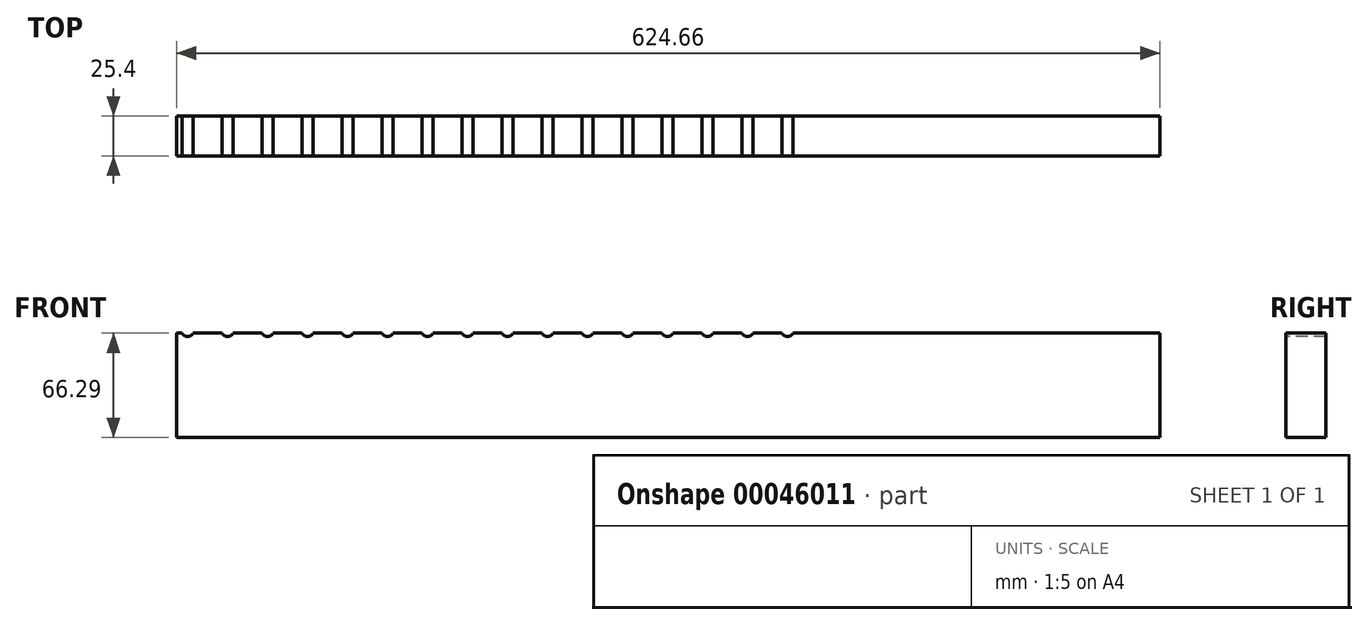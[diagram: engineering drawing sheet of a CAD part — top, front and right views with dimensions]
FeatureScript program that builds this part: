
annotation { "Feature Type Name" : "Feature", "Feature Type Description" : "" }
export const myFeature = defineFeature(function(context is Context, id is Id, definition is map)
    precondition{}
    {
        {
            var Q0;
            Q0=qCreatedBy(makeId("Front.planeOp"),FACE);
            var sketch = newSketch(context, id + "F0", { "sketchPlane" : qUnion([Q0])});
            skLineSegment(sketch, "E0.bottom", {"start": v(-328.43, 0) * mm, "end": v(296.23, 0) * mm});
            skLineSegment(sketch, "E0.top", {"start": v(-328.43, -71.37) * mm, "end": v(296.23, -71.37) * mm});
            skLineSegment(sketch, "E0.left", {"start": v(-328.43, 0) * mm, "end": v(-328.43, -71.37) * mm});
            skLineSegment(sketch, "E0.right", {"start": v(296.23, 0) * mm, "end": v(296.23, -71.37) * mm});
            skSolve(sketch);
        }
        {
            var Q0;
            Q0 = qSketchRegion(id + "F0", true);
            extrude(context, id + "F1", {"entities" : qUnion([Q0]), "depth" : 76.2 * mm});
        }
        {
            var Q0;
            Q0=makeQuery(id+"F1.opExtrude","CAP_EDGE",EDGE,{"disambiguationData":[OSD([sQuery(id+"F0.wireOp",EDGE,"E0.bottom")])],"isStart":false});
            var Q1;
            Q1=makeQuery(id+"F1.opExtrude","CAP_EDGE",EDGE,{"disambiguationData":[OSD([sQuery(id+"F0.wireOp",EDGE,"E0.bottom")])],"isStart":true});
            chamfer(context, id + "F2", {"entities" : qUnion([Q0, Q1]), "width" : 5.08 * mm, "tangentPropagation" : true});
        }
        {
            var Q0;
            Q0=makeQuery(id+"F1.opExtrude","CAP_FACE",FACE,{"disambiguationData":[OSD([sQuery(id+"F0.wireOp",EDGE,"E0.bottom"),sQuery(id+"F0.wireOp",EDGE,"E0.top"),sQuery(id+"F0.wireOp",EDGE,"E0.left"),sQuery(id+"F0.wireOp",EDGE,"E0.right")])],"isStart":false});
            var sketch = newSketch(context, id + "F3", { "sketchPlane" : qUnion([Q0])});
            skCircle(sketch, "E1", {"center": v(-321.3, -35.85) * mm, "radius": 32.55 * mm, "construction": true});
            skLineSegment(sketch, "E2", {"start": v(-321.3, -35.85) * mm, "end": v(-321.3, -3.3) * mm, "construction": true});
            skLineSegment(sketch, "E3", {"start": v(-321.3, -3.3) * mm, "end": v(57.7, -3.3) * mm, "construction": true});
            skLineSegment(sketch, "E4", {"start": v(-321.3, -3.3) * mm, "end": v(-316.3, 0.7) * mm, "construction": true});
            skLineSegment(sketch, "E5", {"start": v(-316.3, 0.7) * mm, "end": v(-325.75, -3.55) * mm, "construction": true});
            skLineSegment(sketch, "E6", {"start": v(-325.75, -3.55) * mm, "end": v(-326.11, -2.75) * mm});
            skLineSegment(sketch, "E7", {"start": v(-321.3, -35.85) * mm, "end": v(-328.43, 0) * mm, "construction": true});
            skArc(sketch, "E8", {"start": v(-328.43, 0) * mm, "mid": v(-337.17, -9.7) * mm, "end": v(-326.11, -2.75) * mm, "construction": true});
            skArc(sketch, "E9", {"start": v(-326.11, -2.75) * mm, "mid": v(-327.08, -1.21) * mm, "end": v(-328.43, 0) * mm});
            skLineSegment(sketch, "E10", {"start": v(-258.56, -152.71) * mm, "end": v(-326.11, -2.75) * mm, "construction": true});
            skArc(sketch, "E11", {"start": v(-325.75, -3.55) * mm, "mid": v(-325.14, -4.7) * mm, "end": v(-324.39, -5.78) * mm});
            skArc(sketch, "E12", {"start": v(-324.39, -5.78) * mm, "mid": v(-307.47, 6.12) * mm, "end": v(-325.75, -3.55) * mm, "construction": true});
            skArc(sketch, "E13.0.MirrorCS", {"start": v(-316.84, -3.55) * mm, "mid": v(-317.45, -4.7) * mm, "end": v(-318.2, -5.78) * mm});
            skLineSegment(sketch, "E14.0.MirrorCS", {"start": v(-316.84, -3.55) * mm, "end": v(-316.48, -2.75) * mm});
            skArc(sketch, "E15.0.MirrorCS", {"start": v(-316.48, -2.75) * mm, "mid": v(-315.51, -1.21) * mm, "end": v(-314.17, 0) * mm});
            skArc(sketch, "E16", {"start": v(-324.39, -5.78) * mm, "mid": v(-321.3, -7.26) * mm, "end": v(-318.2, -5.78) * mm});
            skArc(sketch, "E17", {"start": v(-318.2, -5.78) * mm, "mid": v(-321.3, 0.66) * mm, "end": v(-324.39, -5.78) * mm, "construction": true});
            skArc(sketch, "E18.1.0.0", {"start": v(-300.71, -2.75) * mm, "mid": v(-301.68, -1.21) * mm, "end": v(-303.03, 0) * mm});
            skLineSegment(sketch, "E18.1.0.1", {"start": v(-300.35, -3.55) * mm, "end": v(-300.71, -2.75) * mm});
            skArc(sketch, "E18.1.0.2", {"start": v(-300.35, -3.55) * mm, "mid": v(-299.74, -4.7) * mm, "end": v(-298.99, -5.78) * mm});
            skArc(sketch, "E18.1.0.3", {"start": v(-298.99, -5.78) * mm, "mid": v(-295.9, -7.26) * mm, "end": v(-292.8, -5.78) * mm});
            skArc(sketch, "E18.1.0.4", {"start": v(-291.44, -3.55) * mm, "mid": v(-292.05, -4.7) * mm, "end": v(-292.8, -5.78) * mm});
            skLineSegment(sketch, "E18.1.0.5", {"start": v(-291.44, -3.55) * mm, "end": v(-291.08, -2.75) * mm});
            skArc(sketch, "E18.1.0.6", {"start": v(-291.08, -2.75) * mm, "mid": v(-290.11, -1.21) * mm, "end": v(-288.77, 0) * mm});
            skArc(sketch, "E18.2.0.0", {"start": v(-275.31, -2.75) * mm, "mid": v(-276.28, -1.21) * mm, "end": v(-277.63, 0) * mm});
            skLineSegment(sketch, "E18.2.0.1", {"start": v(-274.95, -3.55) * mm, "end": v(-275.31, -2.75) * mm});
            skArc(sketch, "E18.2.0.2", {"start": v(-274.95, -3.55) * mm, "mid": v(-274.34, -4.7) * mm, "end": v(-273.59, -5.78) * mm});
            skArc(sketch, "E18.2.0.3", {"start": v(-273.59, -5.78) * mm, "mid": v(-270.5, -7.26) * mm, "end": v(-267.4, -5.78) * mm});
            skArc(sketch, "E18.2.0.4", {"start": v(-266.04, -3.55) * mm, "mid": v(-266.65, -4.7) * mm, "end": v(-267.4, -5.78) * mm});
            skLineSegment(sketch, "E18.2.0.5", {"start": v(-266.04, -3.55) * mm, "end": v(-265.68, -2.75) * mm});
            skArc(sketch, "E18.2.0.6", {"start": v(-265.68, -2.75) * mm, "mid": v(-264.71, -1.21) * mm, "end": v(-263.37, 0) * mm});
            skArc(sketch, "E18.3.0.0", {"start": v(-249.91, -2.75) * mm, "mid": v(-250.88, -1.21) * mm, "end": v(-252.23, 0) * mm});
            skLineSegment(sketch, "E18.3.0.1", {"start": v(-249.55, -3.55) * mm, "end": v(-249.91, -2.75) * mm});
            skArc(sketch, "E18.3.0.2", {"start": v(-249.55, -3.55) * mm, "mid": v(-248.94, -4.7) * mm, "end": v(-248.19, -5.78) * mm});
            skArc(sketch, "E18.3.0.3", {"start": v(-248.19, -5.78) * mm, "mid": v(-245.1, -7.26) * mm, "end": v(-242, -5.78) * mm});
            skArc(sketch, "E18.3.0.4", {"start": v(-240.64, -3.55) * mm, "mid": v(-241.25, -4.7) * mm, "end": v(-242, -5.78) * mm});
            skLineSegment(sketch, "E18.3.0.5", {"start": v(-240.64, -3.55) * mm, "end": v(-240.28, -2.75) * mm});
            skArc(sketch, "E18.3.0.6", {"start": v(-240.28, -2.75) * mm, "mid": v(-239.31, -1.21) * mm, "end": v(-237.97, 0) * mm});
            skArc(sketch, "E18.4.0.0", {"start": v(-224.51, -2.75) * mm, "mid": v(-225.48, -1.21) * mm, "end": v(-226.83, 0) * mm});
            skLineSegment(sketch, "E18.4.0.1", {"start": v(-224.15, -3.55) * mm, "end": v(-224.51, -2.75) * mm});
            skArc(sketch, "E18.4.0.2", {"start": v(-224.15, -3.55) * mm, "mid": v(-223.54, -4.7) * mm, "end": v(-222.79, -5.78) * mm});
            skArc(sketch, "E18.4.0.3", {"start": v(-222.79, -5.78) * mm, "mid": v(-219.7, -7.26) * mm, "end": v(-216.6, -5.78) * mm});
            skArc(sketch, "E18.4.0.4", {"start": v(-215.24, -3.55) * mm, "mid": v(-215.85, -4.7) * mm, "end": v(-216.6, -5.78) * mm});
            skLineSegment(sketch, "E18.4.0.5", {"start": v(-215.24, -3.55) * mm, "end": v(-214.88, -2.75) * mm});
            skArc(sketch, "E18.4.0.6", {"start": v(-214.88, -2.75) * mm, "mid": v(-213.91, -1.21) * mm, "end": v(-212.57, 0) * mm});
            skArc(sketch, "E18.5.0.0", {"start": v(-199.11, -2.75) * mm, "mid": v(-200.08, -1.21) * mm, "end": v(-201.43, 0) * mm});
            skLineSegment(sketch, "E18.5.0.1", {"start": v(-198.75, -3.55) * mm, "end": v(-199.11, -2.75) * mm});
            skArc(sketch, "E18.5.0.2", {"start": v(-198.75, -3.55) * mm, "mid": v(-198.14, -4.7) * mm, "end": v(-197.39, -5.78) * mm});
            skArc(sketch, "E18.5.0.3", {"start": v(-197.39, -5.78) * mm, "mid": v(-194.3, -7.26) * mm, "end": v(-191.2, -5.78) * mm});
            skArc(sketch, "E18.5.0.4", {"start": v(-189.84, -3.55) * mm, "mid": v(-190.45, -4.7) * mm, "end": v(-191.2, -5.78) * mm});
            skLineSegment(sketch, "E18.5.0.5", {"start": v(-189.84, -3.55) * mm, "end": v(-189.48, -2.75) * mm});
            skArc(sketch, "E18.5.0.6", {"start": v(-189.48, -2.75) * mm, "mid": v(-188.51, -1.21) * mm, "end": v(-187.17, 0) * mm});
            skArc(sketch, "E18.6.0.0", {"start": v(-173.71, -2.75) * mm, "mid": v(-174.68, -1.21) * mm, "end": v(-176.03, 0) * mm});
            skLineSegment(sketch, "E18.6.0.1", {"start": v(-173.35, -3.55) * mm, "end": v(-173.71, -2.75) * mm});
            skArc(sketch, "E18.6.0.2", {"start": v(-173.35, -3.55) * mm, "mid": v(-172.74, -4.7) * mm, "end": v(-171.99, -5.78) * mm});
            skArc(sketch, "E18.6.0.3", {"start": v(-171.99, -5.78) * mm, "mid": v(-168.9, -7.26) * mm, "end": v(-165.8, -5.78) * mm});
            skArc(sketch, "E18.6.0.4", {"start": v(-164.44, -3.55) * mm, "mid": v(-165.05, -4.7) * mm, "end": v(-165.8, -5.78) * mm});
            skLineSegment(sketch, "E18.6.0.5", {"start": v(-164.44, -3.55) * mm, "end": v(-164.08, -2.75) * mm});
            skArc(sketch, "E18.6.0.6", {"start": v(-164.08, -2.75) * mm, "mid": v(-163.11, -1.21) * mm, "end": v(-161.77, 0) * mm});
            skArc(sketch, "E18.7.0.0", {"start": v(-148.31, -2.75) * mm, "mid": v(-149.28, -1.21) * mm, "end": v(-150.63, 0) * mm});
            skLineSegment(sketch, "E18.7.0.1", {"start": v(-147.95, -3.55) * mm, "end": v(-148.31, -2.75) * mm});
            skArc(sketch, "E18.7.0.2", {"start": v(-147.95, -3.55) * mm, "mid": v(-147.34, -4.7) * mm, "end": v(-146.59, -5.78) * mm});
            skArc(sketch, "E18.7.0.3", {"start": v(-146.59, -5.78) * mm, "mid": v(-143.5, -7.26) * mm, "end": v(-140.4, -5.78) * mm});
            skArc(sketch, "E18.7.0.4", {"start": v(-139.04, -3.55) * mm, "mid": v(-139.65, -4.7) * mm, "end": v(-140.4, -5.78) * mm});
            skLineSegment(sketch, "E18.7.0.5", {"start": v(-139.04, -3.55) * mm, "end": v(-138.68, -2.75) * mm});
            skArc(sketch, "E18.7.0.6", {"start": v(-138.68, -2.75) * mm, "mid": v(-137.71, -1.21) * mm, "end": v(-136.37, 0) * mm});
            skArc(sketch, "E18.8.0.0", {"start": v(-122.91, -2.75) * mm, "mid": v(-123.88, -1.21) * mm, "end": v(-125.23, 0) * mm});
            skLineSegment(sketch, "E18.8.0.1", {"start": v(-122.55, -3.55) * mm, "end": v(-122.91, -2.75) * mm});
            skArc(sketch, "E18.8.0.2", {"start": v(-122.55, -3.55) * mm, "mid": v(-121.94, -4.7) * mm, "end": v(-121.19, -5.78) * mm});
            skArc(sketch, "E18.8.0.3", {"start": v(-121.19, -5.78) * mm, "mid": v(-118.1, -7.26) * mm, "end": v(-115, -5.78) * mm});
            skArc(sketch, "E18.8.0.4", {"start": v(-113.64, -3.55) * mm, "mid": v(-114.25, -4.7) * mm, "end": v(-115, -5.78) * mm});
            skLineSegment(sketch, "E18.8.0.5", {"start": v(-113.64, -3.55) * mm, "end": v(-113.28, -2.75) * mm});
            skArc(sketch, "E18.8.0.6", {"start": v(-113.28, -2.75) * mm, "mid": v(-112.31, -1.21) * mm, "end": v(-110.97, 0) * mm});
            skArc(sketch, "E18.9.0.0", {"start": v(-97.51, -2.75) * mm, "mid": v(-98.48, -1.21) * mm, "end": v(-99.83, 0) * mm});
            skLineSegment(sketch, "E18.9.0.1", {"start": v(-97.15, -3.55) * mm, "end": v(-97.51, -2.75) * mm});
            skArc(sketch, "E18.9.0.2", {"start": v(-97.15, -3.55) * mm, "mid": v(-96.54, -4.7) * mm, "end": v(-95.79, -5.78) * mm});
            skArc(sketch, "E18.9.0.3", {"start": v(-95.79, -5.78) * mm, "mid": v(-92.7, -7.26) * mm, "end": v(-89.6, -5.78) * mm});
            skArc(sketch, "E18.9.0.4", {"start": v(-88.24, -3.55) * mm, "mid": v(-88.85, -4.7) * mm, "end": v(-89.6, -5.78) * mm});
            skLineSegment(sketch, "E18.9.0.5", {"start": v(-88.24, -3.55) * mm, "end": v(-87.88, -2.75) * mm});
            skArc(sketch, "E18.9.0.6", {"start": v(-87.88, -2.75) * mm, "mid": v(-86.91, -1.21) * mm, "end": v(-85.57, 0) * mm});
            skArc(sketch, "E18.10.0.0", {"start": v(-72.11, -2.75) * mm, "mid": v(-73.08, -1.21) * mm, "end": v(-74.43, 0) * mm});
            skLineSegment(sketch, "E18.10.0.1", {"start": v(-71.75, -3.55) * mm, "end": v(-72.11, -2.75) * mm});
            skArc(sketch, "E18.10.0.2", {"start": v(-71.75, -3.55) * mm, "mid": v(-71.14, -4.7) * mm, "end": v(-70.39, -5.78) * mm});
            skArc(sketch, "E18.10.0.3", {"start": v(-70.39, -5.78) * mm, "mid": v(-67.3, -7.26) * mm, "end": v(-64.2, -5.78) * mm});
            skArc(sketch, "E18.10.0.4", {"start": v(-62.84, -3.55) * mm, "mid": v(-63.45, -4.7) * mm, "end": v(-64.2, -5.78) * mm});
            skLineSegment(sketch, "E18.10.0.5", {"start": v(-62.84, -3.55) * mm, "end": v(-62.48, -2.75) * mm});
            skArc(sketch, "E18.10.0.6", {"start": v(-62.48, -2.75) * mm, "mid": v(-61.51, -1.21) * mm, "end": v(-60.17, 0) * mm});
            skArc(sketch, "E18.11.0.0", {"start": v(-46.71, -2.75) * mm, "mid": v(-47.68, -1.21) * mm, "end": v(-49.03, 0) * mm});
            skLineSegment(sketch, "E18.11.0.1", {"start": v(-46.35, -3.55) * mm, "end": v(-46.71, -2.75) * mm});
            skArc(sketch, "E18.11.0.2", {"start": v(-46.35, -3.55) * mm, "mid": v(-45.74, -4.7) * mm, "end": v(-44.99, -5.78) * mm});
            skArc(sketch, "E18.11.0.3", {"start": v(-44.99, -5.78) * mm, "mid": v(-41.9, -7.26) * mm, "end": v(-38.8, -5.78) * mm});
            skArc(sketch, "E18.11.0.4", {"start": v(-37.44, -3.55) * mm, "mid": v(-38.05, -4.7) * mm, "end": v(-38.8, -5.78) * mm});
            skLineSegment(sketch, "E18.11.0.5", {"start": v(-37.44, -3.55) * mm, "end": v(-37.08, -2.75) * mm});
            skArc(sketch, "E18.11.0.6", {"start": v(-37.08, -2.75) * mm, "mid": v(-36.11, -1.21) * mm, "end": v(-34.77, 0) * mm});
            skArc(sketch, "E18.12.0.0", {"start": v(-21.31, -2.75) * mm, "mid": v(-22.28, -1.21) * mm, "end": v(-23.63, 0) * mm});
            skLineSegment(sketch, "E18.12.0.1", {"start": v(-20.95, -3.55) * mm, "end": v(-21.31, -2.75) * mm});
            skArc(sketch, "E18.12.0.2", {"start": v(-20.95, -3.55) * mm, "mid": v(-20.34, -4.7) * mm, "end": v(-19.59, -5.78) * mm});
            skArc(sketch, "E18.12.0.3", {"start": v(-19.59, -5.78) * mm, "mid": v(-16.5, -7.26) * mm, "end": v(-13.4, -5.78) * mm});
            skArc(sketch, "E18.12.0.4", {"start": v(-12.04, -3.55) * mm, "mid": v(-12.65, -4.7) * mm, "end": v(-13.4, -5.78) * mm});
            skLineSegment(sketch, "E18.12.0.5", {"start": v(-12.04, -3.55) * mm, "end": v(-11.68, -2.75) * mm});
            skArc(sketch, "E18.12.0.6", {"start": v(-11.68, -2.75) * mm, "mid": v(-10.71, -1.21) * mm, "end": v(-9.37, 0) * mm});
            skArc(sketch, "E18.13.0.0", {"start": v(4.09, -2.75) * mm, "mid": v(3.12, -1.21) * mm, "end": v(1.77, 0) * mm});
            skLineSegment(sketch, "E18.13.0.1", {"start": v(4.45, -3.55) * mm, "end": v(4.09, -2.75) * mm});
            skArc(sketch, "E18.13.0.2", {"start": v(4.45, -3.55) * mm, "mid": v(5.06, -4.7) * mm, "end": v(5.81, -5.78) * mm});
            skArc(sketch, "E18.13.0.3", {"start": v(5.81, -5.78) * mm, "mid": v(8.9, -7.26) * mm, "end": v(12, -5.78) * mm});
            skArc(sketch, "E18.13.0.4", {"start": v(13.36, -3.55) * mm, "mid": v(12.75, -4.7) * mm, "end": v(12, -5.78) * mm});
            skLineSegment(sketch, "E18.13.0.5", {"start": v(13.36, -3.55) * mm, "end": v(13.72, -2.75) * mm});
            skArc(sketch, "E18.13.0.6", {"start": v(13.72, -2.75) * mm, "mid": v(14.69, -1.21) * mm, "end": v(16.03, 0) * mm});
            skArc(sketch, "E18.14.0.0", {"start": v(29.49, -2.75) * mm, "mid": v(28.52, -1.21) * mm, "end": v(27.17, 0) * mm});
            skLineSegment(sketch, "E18.14.0.1", {"start": v(29.85, -3.55) * mm, "end": v(29.49, -2.75) * mm});
            skArc(sketch, "E18.14.0.2", {"start": v(29.85, -3.55) * mm, "mid": v(30.46, -4.7) * mm, "end": v(31.21, -5.78) * mm});
            skArc(sketch, "E18.14.0.3", {"start": v(31.21, -5.78) * mm, "mid": v(34.3, -7.26) * mm, "end": v(37.4, -5.78) * mm});
            skArc(sketch, "E18.14.0.4", {"start": v(38.76, -3.55) * mm, "mid": v(38.15, -4.7) * mm, "end": v(37.4, -5.78) * mm});
            skLineSegment(sketch, "E18.14.0.5", {"start": v(38.76, -3.55) * mm, "end": v(39.12, -2.75) * mm});
            skArc(sketch, "E18.14.0.6", {"start": v(39.12, -2.75) * mm, "mid": v(40.09, -1.21) * mm, "end": v(41.43, 0) * mm});
            skArc(sketch, "E18.15.0.0", {"start": v(54.89, -2.75) * mm, "mid": v(53.92, -1.21) * mm, "end": v(52.57, 0) * mm});
            skLineSegment(sketch, "E18.15.0.1", {"start": v(55.25, -3.55) * mm, "end": v(54.89, -2.75) * mm});
            skArc(sketch, "E18.15.0.2", {"start": v(55.25, -3.55) * mm, "mid": v(55.86, -4.7) * mm, "end": v(56.61, -5.78) * mm});
            skArc(sketch, "E18.15.0.3", {"start": v(56.61, -5.78) * mm, "mid": v(59.7, -7.26) * mm, "end": v(62.8, -5.78) * mm});
            skArc(sketch, "E18.15.0.4", {"start": v(64.16, -3.55) * mm, "mid": v(63.55, -4.7) * mm, "end": v(62.8, -5.78) * mm});
            skLineSegment(sketch, "E18.15.0.5", {"start": v(64.16, -3.55) * mm, "end": v(64.52, -2.75) * mm});
            skArc(sketch, "E18.15.0.6", {"start": v(64.52, -2.75) * mm, "mid": v(65.49, -1.21) * mm, "end": v(66.83, 0) * mm});
            skLineSegment(sketch, "E18.direction1", {"start": v(-332.12, -5.46) * mm, "end": v(-306.72, -5.46) * mm, "construction": true});
            skSolve(sketch);
        }
        {
            var Q0;
            {var subQ72=sQuery(id+"F3.wireOp",EDGE,"E16");Q0=makeQuery(id+"F3.imprint","IMPRINT",FACE,{"disambiguationData":[TD([[makeQuery(id+"F3.imprint","IMPRINT",EDGE,{"derivedFrom":subQ72}),-1.0]])]});}
            extrude(context, id + "F4", {"entities" : qUnion([Q0]), "operationType" : NewBodyOperationType.INTERSECT, "oppositeDirection" : true, "depth" : 25.4 * mm});
        }
    });
